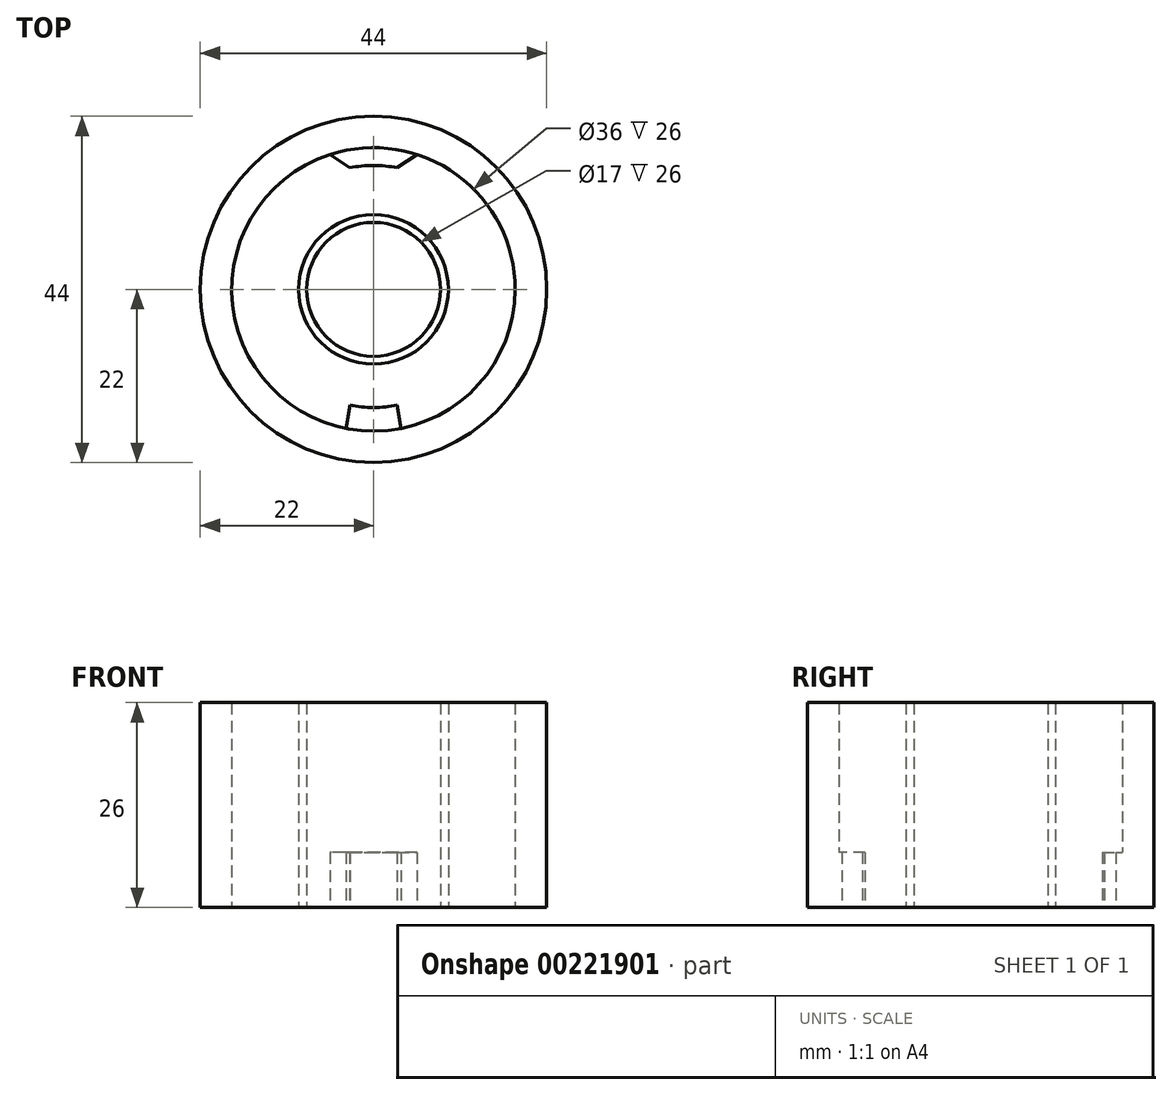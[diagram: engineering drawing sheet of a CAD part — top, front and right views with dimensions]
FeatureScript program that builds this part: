
annotation { "Feature Type Name" : "Feature", "Feature Type Description" : "" }
export const myFeature = defineFeature(function(context is Context, id is Id, definition is map)
    precondition{}
    {
        {
            var Q0;
            Q0=qCreatedBy(makeId("Top.planeOp"),FACE);
            var sketch = newSketch(context, id + "F0", { "sketchPlane" : qUnion([Q0])});
            skCircle(sketch, "E0", {"center": v(0, 0) * mm, "radius": 18 * mm});
            skCircle(sketch, "E1", {"center": v(0, 0) * mm, "radius": 9.5 * mm});
            skLineSegment(sketch, "E2", {"start": v(3.03, 15.44) * mm, "end": v(5.5, 17.14) * mm});
            skLineSegment(sketch, "E3", {"start": v(-3.03, 15.44) * mm, "end": v(-5.5, 17.14) * mm});
            skLineSegment(sketch, "E4", {"start": v(3.03, 15.44) * mm, "end": v(3.03, 14.95) * mm, "construction": true});
            skLineSegment(sketch, "E5", {"start": v(3.03, 14.95) * mm, "end": v(0, 14.95) * mm, "construction": true});
            skLineSegment(sketch, "E6", {"start": v(-3.03, 15.44) * mm, "end": v(-3.03, 14.95) * mm, "construction": true});
            skLineSegment(sketch, "E7", {"start": v(-3.03, 14.95) * mm, "end": v(0, 14.95) * mm, "construction": true});
            skLineSegment(sketch, "E8", {"start": v(5.5, 17.14) * mm, "end": v(0, 17.14) * mm, "construction": true});
            skLineSegment(sketch, "E9", {"start": v(0, 17.14) * mm, "end": v(-5.5, 17.14) * mm, "construction": true});
            skArc(sketch, "E10", {"start": v(3.03, 15.44) * mm, "mid": v(0, 15.74) * mm, "end": v(-3.03, 15.44) * mm});
            skLineSegment(sketch, "E11", {"start": v(3, -14.7) * mm, "end": v(3.5, -17.66) * mm});
            skLineSegment(sketch, "E12", {"start": v(-3, -14.7) * mm, "end": v(-3.5, -17.66) * mm});
            skLineSegment(sketch, "E13", {"start": v(-3.5, -17.66) * mm, "end": v(0, -17.66) * mm, "construction": true});
            skLineSegment(sketch, "E14", {"start": v(0, -17.66) * mm, "end": v(3.5, -17.66) * mm, "construction": true});
            skLineSegment(sketch, "E15", {"start": v(-3, -14.7) * mm, "end": v(-3, -12.96) * mm, "construction": true});
            skLineSegment(sketch, "E16", {"start": v(-3, -12.96) * mm, "end": v(0, -12.96) * mm, "construction": true});
            skLineSegment(sketch, "E17", {"start": v(0, -12.96) * mm, "end": v(3, -12.96) * mm, "construction": true});
            skLineSegment(sketch, "E18", {"start": v(3, -12.96) * mm, "end": v(3, -14.7) * mm, "construction": true});
            skArc(sketch, "E19", {"start": v(-3, -14.7) * mm, "mid": v(0, -15) * mm, "end": v(3, -14.7) * mm});
            skCircle(sketch, "E20", {"center": v(0, 0) * mm, "radius": 8.5 * mm});
            skCircle(sketch, "E21", {"center": v(0, 0) * mm, "radius": 22 * mm});
            skSolve(sketch);
        }
        {
            var Q0;
            Q0=makeQuery(id+"F0.imprint","IMPRINT",FACE,{"disambiguationData":[TD([[makeQuery(id+"F0.imprint","IMPRINT",EDGE,{"derivedFrom":sQuery(id+"F0.wireOp",EDGE,"E21")}),1.0]])]});
            var Q1;
            Q1=makeQuery(id+"F0.imprint","IMPRINT",FACE,{"disambiguationData":[TD([[makeQuery(id+"F0.imprint","IMPRINT",EDGE,{"derivedFrom":sQuery(id+"F0.wireOp",EDGE,"E1")}),1.0]])]});
            extrude(context, id + "F1", {"entities" : qUnion([Q0, Q1]), "depth" : 26 * mm});
        }
        {
            var Q0;
            {var subQ0=sQuery(id+"F0.wireOp",EDGE,"E2");Q0=makeQuery(id+"F0.imprint","IMPRINT",FACE,{"disambiguationData":[TD([[makeQuery(id+"F0.imprint","IMPRINT",EDGE,{"derivedFrom":subQ0}),1.0]])]});}
            var Q1;
            {var subQ0=sQuery(id+"F0.wireOp",EDGE,"E11");Q1=makeQuery(id+"F0.imprint","IMPRINT",FACE,{"disambiguationData":[TD([[makeQuery(id+"F0.imprint","IMPRINT",EDGE,{"derivedFrom":subQ0}),-1.0]])]});}
            extrude(context, id + "F2", {"entities" : qUnion([Q0, Q1]), "operationType" : NewBodyOperationType.ADD, "depth" : 7 * mm});
        }
    });
